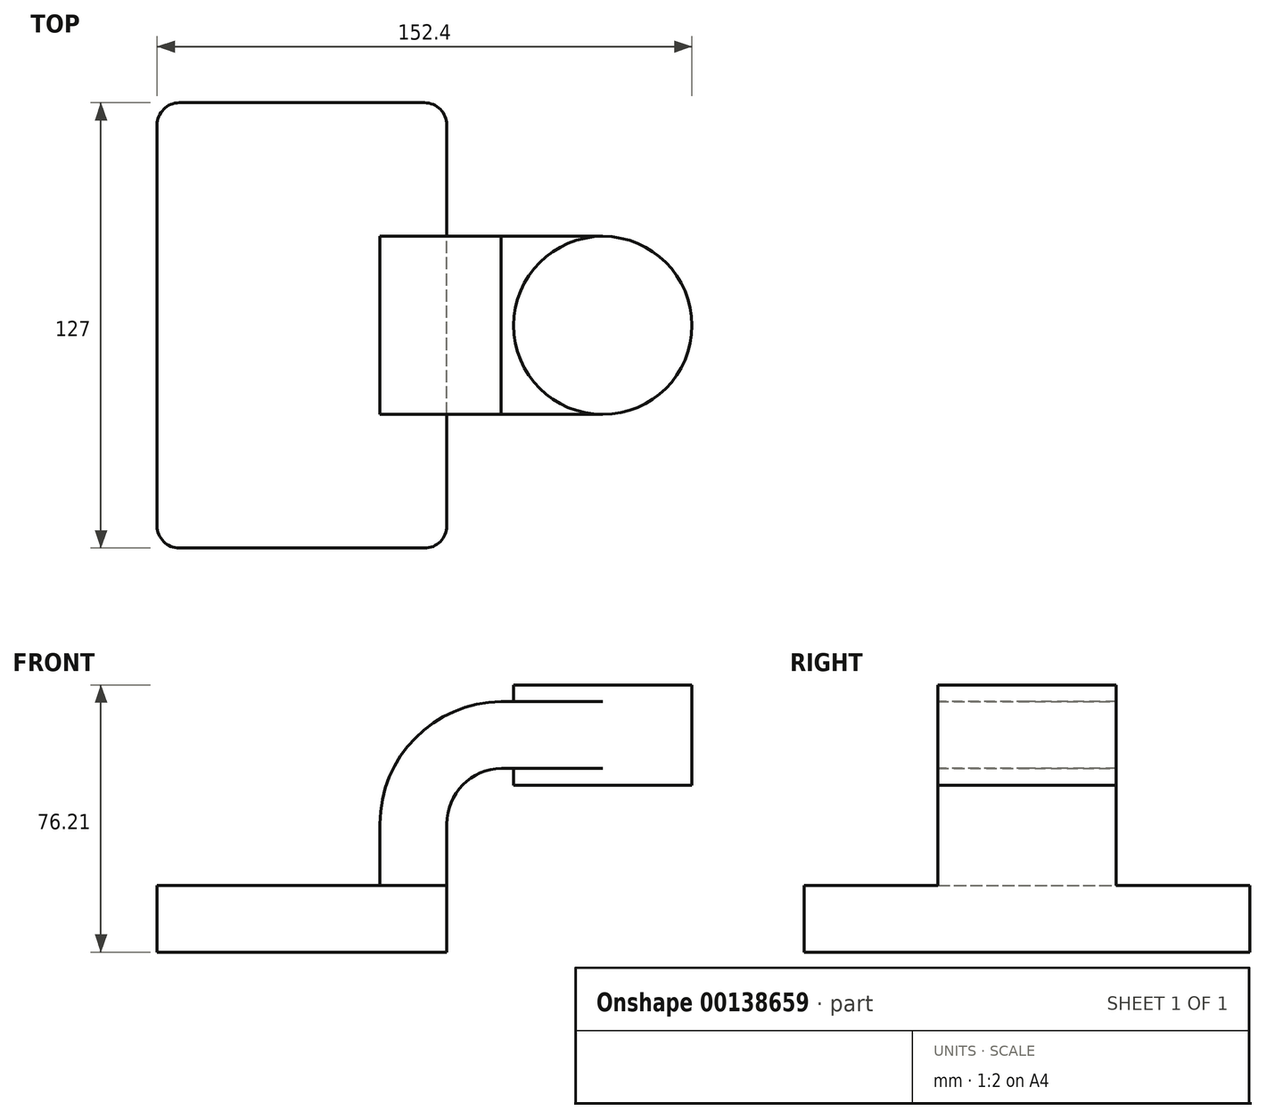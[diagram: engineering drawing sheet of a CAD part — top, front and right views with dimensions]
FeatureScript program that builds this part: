
annotation { "Feature Type Name" : "Feature", "Feature Type Description" : "" }
export const myFeature = defineFeature(function(context is Context, id is Id, definition is map)
    precondition{}
    {
        {
            var Q0;
            Q0=qCreatedBy(makeId("Front.planeOp"),FACE);
            var sketch = newSketch(context, id + "F0", { "sketchPlane" : qUnion([Q0])});
            skLineSegment(sketch, "E0.bottom", {"start": v(-41.28, -9.53) * mm, "end": v(41.28, -9.53) * mm});
            skLineSegment(sketch, "E0.top", {"start": v(-41.28, 9.53) * mm, "end": v(41.28, 9.53) * mm});
            skLineSegment(sketch, "E0.left", {"start": v(-41.28, -9.53) * mm, "end": v(-41.28, 9.53) * mm});
            skLineSegment(sketch, "E0.right", {"start": v(41.28, -9.53) * mm, "end": v(41.28, 9.52) * mm});
            skPoint(sketch, "E0.middle", {"position": v(0, 0) * mm});
            skLineSegment(sketch, "E1.bottom", {"start": v(60.32, 38.1) * mm, "end": v(111.12, 38.1) * mm});
            skLineSegment(sketch, "E1.top", {"start": v(60.32, 66.67) * mm, "end": v(111.12, 66.67) * mm});
            skLineSegment(sketch, "E1.left", {"start": v(60.32, 38.1) * mm, "end": v(60.32, 66.67) * mm});
            skLineSegment(sketch, "E1.right", {"start": v(111.12, 38.1) * mm, "end": v(111.12, 66.68) * mm});
            skLineSegment(sketch, "E2", {"start": v(41.28, 9.52) * mm, "end": v(41.28, 27) * mm});
            skArc(sketch, "E3", {"start": v(41.27, 27) * mm, "mid": v(45.83, 38.13) * mm, "end": v(56.87, 42.88) * mm});
            skLineSegment(sketch, "E4", {"start": v(56.87, 42.88) * mm, "end": v(85.72, 42.88) * mm});
            skLineSegment(sketch, "E5.0", {"start": v(56.73, 61.93) * mm, "end": v(85.72, 61.93) * mm});
            skArc(sketch, "E5.1", {"start": v(22.23, 27) * mm, "mid": v(32.3, 51.55) * mm, "end": v(56.73, 61.93) * mm});
            skLineSegment(sketch, "E5.2", {"start": v(22.23, 9.52) * mm, "end": v(22.23, 27) * mm});
            skLineSegment(sketch, "E6", {"start": v(85.72, 38.1) * mm, "end": v(85.72, 66.68) * mm});
            skFitSpline(sketch, "E7", {"points": [v(-41.28, 9.52) * mm, v(56.73, 61.93) * mm], "startDerivative": vector(0.83, 97.38) * mm, "endDerivative": vector(137.42, -0.4) * mm});
            skSolve(sketch);
        }
        {
            var Q0;
            Q0=makeQuery(id+"F0.imprint","IMPRINT",FACE,{"disambiguationData":[TD([[makeQuery(id+"F0.imprint","IMPRINT",EDGE,{"derivedFrom":sQuery(id+"F0.wireOp",EDGE,"E0.bottom")}),1.0]])]});
            extrude(context, id + "F1", {"entities" : qUnion([Q0]), "endBound" : BoundingType.SYMMETRIC, "depth" : 127 * mm});
        }
        {
            var Q0;
            {var subQ0=sQuery(id+"F0.wireOp",EDGE,"E4");var subQ1=sQuery(id+"F0.wireOp",EDGE,"E1.left");var subQ2=makeQuery(id+"F0.imprint","INTERSECT",VERTEX,{"derivedFrom":[subQ1,subQ0]});Q0=makeQuery(id+"F0.imprint","IMPRINT",FACE,{"disambiguationData":[TD([[makeQuery(id+"F0.imprint","IMPRINT",EDGE,{"disambiguationData":[TD([[subQ2,-1.0]])],"derivedFrom":subQ1}),-1.0]])]});}
            var Q1;
            {var subQ1=sQuery(id+"F0.wireOp",EDGE,"E2");Q1=makeQuery(id+"F0.imprint","IMPRINT",FACE,{"disambiguationData":[TD([[makeQuery(id+"F0.imprint","IMPRINT",EDGE,{"derivedFrom":subQ1}),1.0]])]});}
            extrude(context, id + "F2", {"entities" : qUnion([Q0, Q1]), "operationType" : NewBodyOperationType.ADD, "endBound" : BoundingType.SYMMETRIC, "depth" : 50.8 * mm});
        }
        {
            var Q0;
            Q0=makeQuery(id+"F0.imprint","IMPRINT",FACE,{"disambiguationData":[TD([[makeQuery(id+"F0.imprint","IMPRINT",EDGE,{"derivedFrom":sQuery(id+"F0.wireOp",EDGE,"E5.1")}),1.0]])]});
            extrude(context, id + "F3", {"entities" : qUnion([Q0]), "operationType" : NewBodyOperationType.ADD, "endBound" : BoundingType.SYMMETRIC, "depth" : 15.88 * mm});
        }
        {
            var Q0;
            {var subQ0=sQuery(id+"F0.wireOp",EDGE,"E1.right");Q0=makeQuery(id+"F0.imprint","IMPRINT",FACE,{"disambiguationData":[TD([[makeQuery(id+"F0.imprint","IMPRINT",EDGE,{"derivedFrom":subQ0}),1.0]])]});}
            var Q1;
            Q1=sQuery(id+"F0.wireOp",EDGE,"E6");
            revolve(context, id + "F4", {"operationType" : NewBodyOperationType.ADD, "entities" : qUnion([Q0]), "axis" : qUnion([Q1]), "revolveType" : RevolveType.FULL});
        }
        {
            var Q0;
            Q0=makeQuery(id+"F1.opExtrude","CAP_EDGE",EDGE,{"disambiguationData":[OSD([sQuery(id+"F0.wireOp",EDGE,"E0.left")])],"isStart":false});
            var Q1;
            Q1=makeQuery(id+"F1.opExtrude","CAP_EDGE",EDGE,{"disambiguationData":[OSD([sQuery(id+"F0.wireOp",EDGE,"E0.right")])],"isStart":false});
            var Q2;
            Q2=makeQuery(id+"F1.opExtrude","CAP_EDGE",EDGE,{"disambiguationData":[OSD([sQuery(id+"F0.wireOp",EDGE,"E0.right")])],"isStart":true});
            var Q3;
            Q3=makeQuery(id+"F1.opExtrude","CAP_EDGE",EDGE,{"disambiguationData":[OSD([sQuery(id+"F0.wireOp",EDGE,"E0.left")])],"isStart":true});
            fillet(context, id + "F5", {"entities" : qUnion([Q0, Q1, Q2, Q3]), "radius" : 6.35 * mm, "tangentPropagation" : true, "allowEdgeOverflow" : false});
        }
    });
